# Revit family: Outdoor-Kitchen-Equipment_Kalamazoo_Dual-Zone-Cold-Cabinets_Arcadia
name_source: partatom
category: Specialty Equipment
revit_build: Autodesk Revit 2018 (Build: 20190510_1515(x64)
units: mm (PartAtom-declared; Revit-internal decimal feet)

## family parameters
Always vertical = Yes
Cut with Voids When Loaded = No
OmniClass Number = 23.40.40.11.24
OmniClass Title = Cold Cabinets
Part Type = Normal
Room Calculation Point = No
Round Connector Dimension = Use Diameter
Shared = No
Work Plane-Based = No

## types (3) — shared parameters
Apparent Load = 74 VA
Assembly Code = E1090300
Current = 2 A
Depth = 24"
Frequency = 60 Hz
Height = 34 3/8"
Keynote = 11400
Manufacturer = Kalamazoo Outdoor Gourmet
Number of Poles = 3
Power Factor = 0.8
Product Material = Kalamazoo - Stainless Steel - 304 OR 316L
Product data url = https://www.bimobject.com
Total Cooling Capacity = 1985.0 Btu/h
URL = https://kalamazoogourmet.com
Voltage = 120 V
Weight (lb) = 215.00 lbf
Width = 23 7/8"

## per-type parameters (varying)
| type | 6KD | Description |
| K-HP24CO-2KD | No | Arcadia 24-inch Dual-Zone Refrigerator and Wine Chiller |
| K-HP24ZO-6KD | Yes | Arcadia 24-inch Outdoor Refrigerator and Freezer Drawers |
| K-HP24DO-2KD | No | Arcadia 24-inch Dual-Zone Wine Chiller |

note: column(s) folded — value = type name in every type: Model

## geometry (parser evidence)
native form markers: Sweep x2
no freeform markers — native parametric forms only
